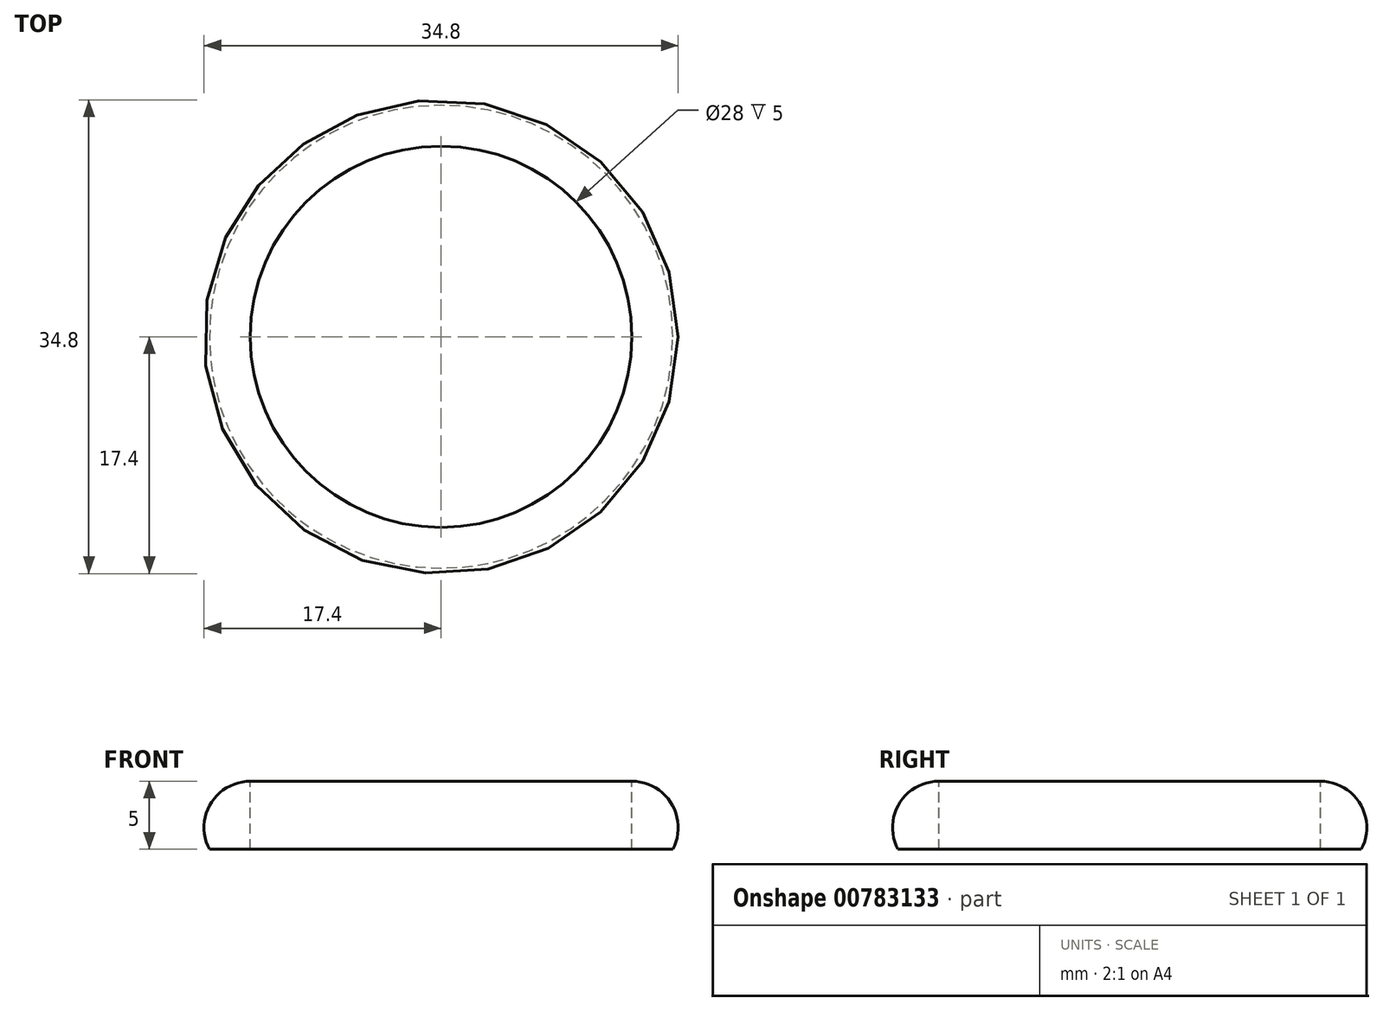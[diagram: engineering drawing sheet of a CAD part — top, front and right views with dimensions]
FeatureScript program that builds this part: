
annotation { "Feature Type Name" : "Feature", "Feature Type Description" : "" }
export const myFeature = defineFeature(function(context is Context, id is Id, definition is map)
    precondition{}
    {
        {
            var Q0;
            Q0=qCreatedBy(makeId("Front.planeOp"),FACE);
            var sketch = newSketch(context, id + "F0", { "sketchPlane" : qUnion([Q0])});
            skLineSegment(sketch, "E0", {"start": v(0, 0) * mm, "end": v(17, 0) * mm});
            skLineSegment(sketch, "E1", {"start": v(0, 5) * mm, "end": v(0, 0) * mm});
            skLineSegment(sketch, "E2", {"start": v(0, 5) * mm, "end": v(14, 5) * mm});
            skArc(sketch, "E3", {"start": v(17, 0) * mm, "mid": v(16.92, 3.35) * mm, "end": v(14, 5) * mm});
            skSolve(sketch);
        }
        {
            var Q0;
            Q0=makeQuery(id+"F0.imprint","IMPRINT",FACE,{"disambiguationData":[TD([[makeQuery(id+"F0.imprint","IMPRINT",EDGE,{"derivedFrom":sQuery(id+"F0.wireOp",EDGE,"E0")}),1.0]])]});
            var Q1;
            Q1=sQuery(id+"F0.wireOp",EDGE,"E1");
            revolve(context, id + "F1", {"surfaceOperationType" : NewSurfaceOperationType.NEW, "entities" : qUnion([Q0]), "axis" : qUnion([Q1]), "revolveType" : RevolveType.FULL});
        }
        {
            var Q0;
            Q0=makeQuery(id+"F1.opRevolve","SWEPT_FACE",FACE,{"disambiguationData":[OSD([sQuery(id+"F0.wireOp",EDGE,"E2")])]});
            var sketch = newSketch(context, id + "F2", { "sketchPlane" : qUnion([Q0])});
            skCircle(sketch, "E4", {"center": v(0, 0) * mm, "radius": 14 * mm});
            skSolve(sketch);
        }
        {
            var Q0;
            Q0=makeQuery(id+"F2.imprint","IMPRINT",FACE,{"disambiguationData":[TD([[makeQuery(id+"F2.imprint","IMPRINT",EDGE,{"derivedFrom":sQuery(id+"F2.wireOp",EDGE,"E4")}),1.0]])]});
            extrude(context, id + "F3", {"entities" : qUnion([Q0]), "operationType" : NewBodyOperationType.REMOVE, "oppositeDirection" : true, "depth" : 25 * mm, "offsetDistance" : 25 * mm});
        }
    });
